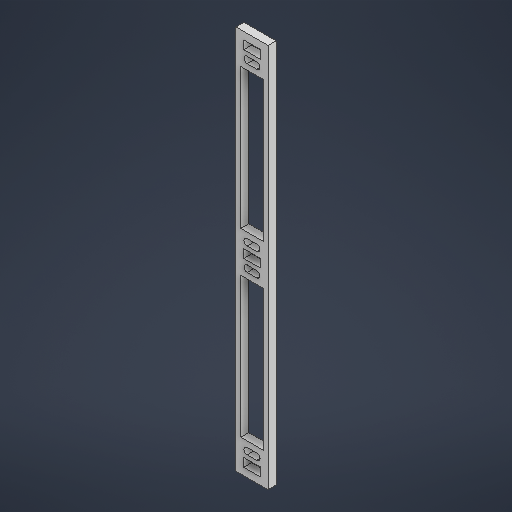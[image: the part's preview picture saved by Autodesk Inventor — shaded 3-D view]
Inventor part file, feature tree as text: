
AUTODESK INVENTOR PART (.ipt)
format: ipt  version: 2025.3 (Build 293356000, 356)  size: 267,264 bytes
history: native  units: mm
features: extrude x1, sketch x1
ambient origin geometry x8: Origin, YZ Plane, XZ Plane, XY Plane, X Axis, Y Axis, Z Axis, Center Point
bodies: Body1 (feature_tree)
feature tree (2):
  extrude  "Extrusion3"  Depth=20.0mm
  sketch  "Sketch1"  dims[d0=240.0mm d1=20.0mm d2=10.3mm d3=5.3mm d4=107.5mm d5=5.3mm d6=4.85mm d7=4.85mm d10=2.0mm d11=2.5mm d12=7.0mm d13=7.0mm d14=2.5mm d15=2.0mm d16=7.0mm d17=7.0mm d18=2.0mm d19=6.0mm d20=7.0mm d21=2.5mm d22=2.5mm d23=2.0mm d24=7.0mm d25=7.0mm d28=3.5mm d29=3.5mm d30=3.0mm d31=3.0mm d32=3.5mm d33=3.5mm d34=3.0mm d35=3.0mm d36=5.0mm d37=0.0mm]
